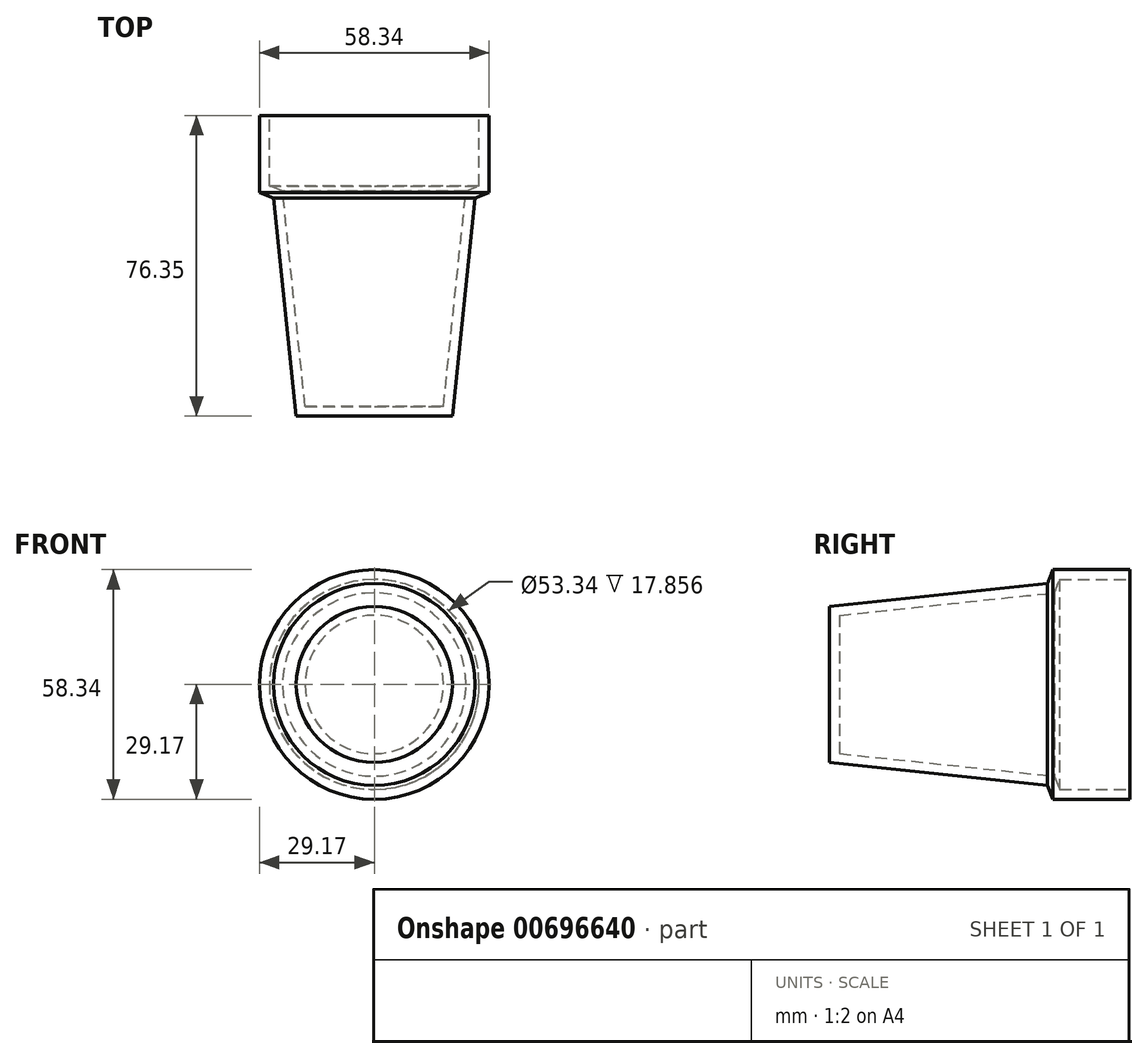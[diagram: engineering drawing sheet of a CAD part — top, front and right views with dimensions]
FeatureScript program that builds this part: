
annotation { "Feature Type Name" : "Feature", "Feature Type Description" : "" }
export const myFeature = defineFeature(function(context is Context, id is Id, definition is map)
    precondition{}
    {
        {
            var Q0;
            Q0=qCreatedBy(makeId("Top.planeOp"),FACE);
            var sketch = newSketch(context, id + "F0", { "sketchPlane" : qUnion([Q0])});
            skLineSegment(sketch, "E0", {"start": v(0, 76.2) * mm, "end": v(0, -75.58) * mm});
            skLineSegment(sketch, "E1", {"start": v(0, -55.43) * mm, "end": v(19.82, -55.43) * mm});
            skLineSegment(sketch, "E2", {"start": v(19.82, -55.43) * mm, "end": v(25.63, 0) * mm});
            skLineSegment(sketch, "E3", {"start": v(25.63, 0) * mm, "end": v(29.17, 1.33) * mm});
            skLineSegment(sketch, "E4", {"start": v(29.17, 1.33) * mm, "end": v(29.17, 20.92) * mm});
            skLineSegment(sketch, "E5", {"start": v(29.17, 20.92) * mm, "end": v(0, 20.92) * mm});
            skSolve(sketch);
        }
        {
            var Q0;
            {var subQ0=sQuery(id+"F0.wireOp",EDGE,"E1");Q0=makeQuery(id+"F0.imprint","IMPRINT",FACE,{"disambiguationData":[TD([[makeQuery(id+"F0.imprint","IMPRINT",EDGE,{"derivedFrom":subQ0}),1.0]])]});}
            var Q1;
            Q1=sQuery(id+"F0.wireOp",EDGE,"E0");
            revolve(context, id + "F1", {"entities" : qUnion([Q0]), "axis" : qUnion([Q1]), "revolveType" : RevolveType.FULL});
        }
        {
            var Q0;
            Q0=makeQuery(id+"F1.opRevolve","SWEPT_FACE",FACE,{"disambiguationData":[OSD([sQuery(id+"F0.wireOp",EDGE,"E5")])]});
            shell(context, id + "F2", {"entities" : qUnion([Q0]), "thickness" : 2.5 * mm});
        }
    });
